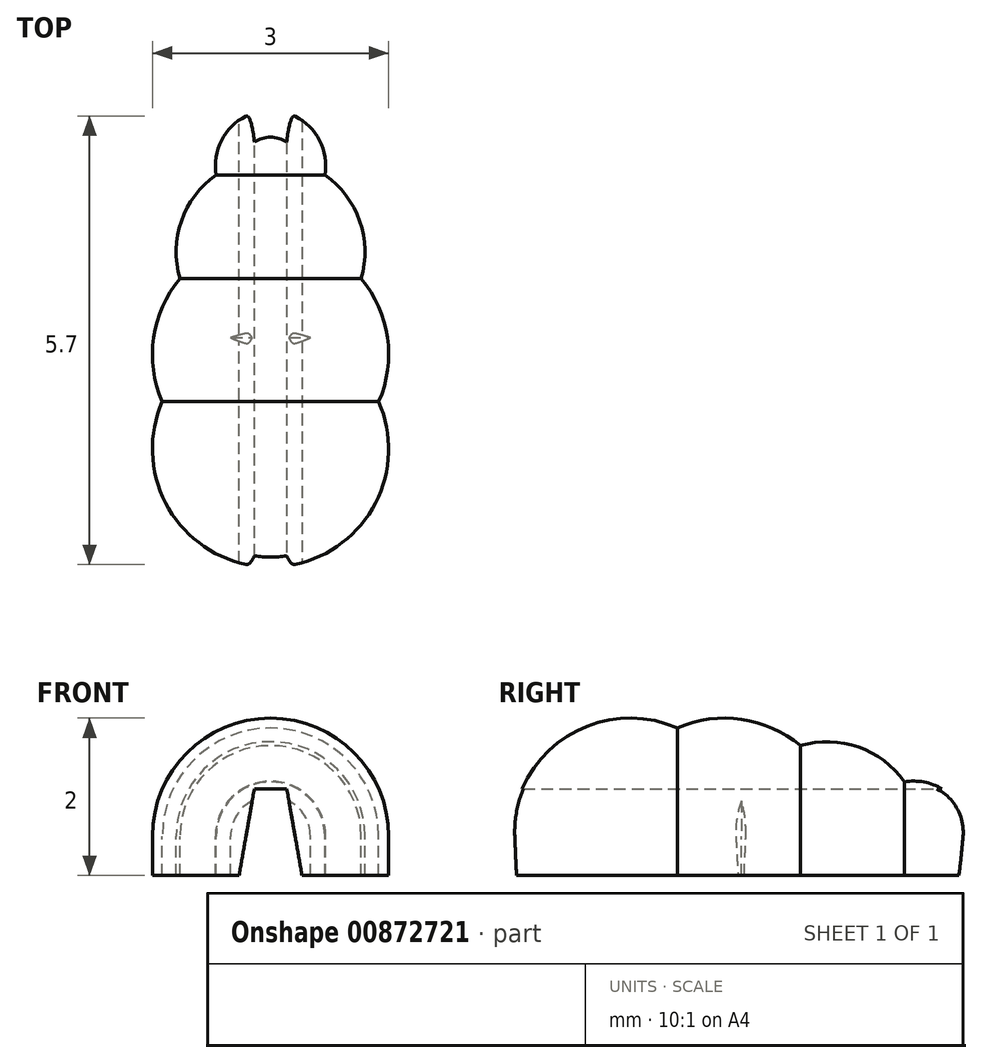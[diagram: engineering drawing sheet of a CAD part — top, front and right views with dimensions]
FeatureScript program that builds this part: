
annotation { "Feature Type Name" : "Feature", "Feature Type Description" : "" }
export const myFeature = defineFeature(function(context is Context, id is Id, definition is map)
    precondition{}
    {
        {
            var Q0;
            Q0=qCreatedBy(makeId("Top.planeOp"),FACE);
            var sketch = newSketch(context, id + "F0", { "sketchPlane" : qUnion([Q0])});
            skArc(sketch, "E0", {"start": v(0, -1.5) * mm, "mid": v(1.5, 0) * mm, "end": v(0, 1.5) * mm});
            skArc(sketch, "E1", {"start": v(0, -2.7) * mm, "mid": v(1.5, -1.2) * mm, "end": v(0, 0.3) * mm});
            skLineSegment(sketch, "E2", {"start": v(0, 3.1) * mm, "end": v(0, -4.3) * mm});
            skArc(sketch, "E3", {"start": v(0, 0.1) * mm, "mid": v(1.2, 1.3) * mm, "end": v(0, 2.5) * mm});
            skArc(sketch, "E4", {"start": v(0, -3.7) * mm, "mid": v(1.2, -2.5) * mm, "end": v(0, -1.3) * mm});
            skArc(sketch, "E5", {"start": v(0, 1.7) * mm, "mid": v(0.7, 2.4) * mm, "end": v(0, 3.1) * mm});
            skArc(sketch, "E6", {"start": v(0, -4.3) * mm, "mid": v(0.7, -3.6) * mm, "end": v(0, -2.9) * mm});
            skSolve(sketch);
        }
        {
            var Q0;
            {var subQ0=sQuery(id+"F0.wireOp",EDGE,"E2");var subQ1=sQuery(id+"F0.wireOp",EDGE,"E0");var subQ2=makeQuery(id+"F0.imprint","INTERSECT",VERTEX,{"disambiguationData":[OD(1.0)],"derivedFrom":[subQ1,subQ0]});Q0=makeQuery(id+"F0.imprint","IMPRINT",FACE,{"disambiguationData":[TD([[makeQuery(id+"F0.imprint","IMPRINT",EDGE,{"disambiguationData":[TD([[subQ2,1.0]])],"derivedFrom":subQ1}),1.0]])]});}
            var Q1;
            {var subQ0=sQuery(id+"F0.wireOp",EDGE,"E2");var subQ1=sQuery(id+"F0.wireOp",EDGE,"E0");var subQ2=makeQuery(id+"F0.imprint","INTERSECT",VERTEX,{"disambiguationData":[OD(0.0)],"derivedFrom":[subQ1,subQ0]});Q1=makeQuery(id+"F0.imprint","IMPRINT",FACE,{"disambiguationData":[TD([[makeQuery(id+"F0.imprint","IMPRINT",EDGE,{"disambiguationData":[TD([[subQ2,-1.0]])],"derivedFrom":subQ1}),1.0]])]});}
            var Q2;
            {var subQ0=sQuery(id+"F0.wireOp",EDGE,"E2");var subQ1=sQuery(id+"F0.wireOp",EDGE,"E0");var subQ2=makeQuery(id+"F0.imprint","INTERSECT",VERTEX,{"disambiguationData":[OD(0.0)],"derivedFrom":[subQ1,subQ0]});Q2=makeQuery(id+"F0.imprint","IMPRINT",FACE,{"disambiguationData":[TD([[makeQuery(id+"F0.imprint","IMPRINT",EDGE,{"disambiguationData":[TD([[subQ2,-1.0]])],"derivedFrom":subQ1}),-1.0]])]});}
            var Q3;
            {var subQ0=sQuery(id+"F0.wireOp",EDGE,"E2");var subQ1=sQuery(id+"F0.wireOp",EDGE,"E0");var subQ2=makeQuery(id+"F0.imprint","INTERSECT",VERTEX,{"disambiguationData":[OD(1.0)],"derivedFrom":[subQ1,subQ0]});Q3=makeQuery(id+"F0.imprint","IMPRINT",FACE,{"disambiguationData":[TD([[makeQuery(id+"F0.imprint","IMPRINT",EDGE,{"disambiguationData":[TD([[subQ2,1.0]])],"derivedFrom":subQ1}),-1.0]])]});}
            var Q4;
            {var subQ0=sQuery(id+"F0.wireOp",EDGE,"E1");var subQ1=sQuery(id+"F0.wireOp",EDGE,"E0");var subQ2=makeQuery(id+"F0.imprint","INTERSECT",VERTEX,{"derivedFrom":[subQ1,subQ0]});Q4=makeQuery(id+"F0.imprint","IMPRINT",FACE,{"disambiguationData":[TD([[makeQuery(id+"F0.imprint","IMPRINT",EDGE,{"disambiguationData":[TD([[subQ2,-1.0]])],"derivedFrom":subQ1}),1.0]])]});}
            var Q5;
            {var subQ3=sQuery(id+"F0.wireOp",EDGE,"E1");var subQ7=sQuery(id+"F0.wireOp",EDGE,"E0");var subQ8=makeQuery(id+"F0.imprint","INTERSECT",VERTEX,{"derivedFrom":[subQ7,subQ3]});Q5=makeQuery(id+"F0.imprint","IMPRINT",FACE,{"disambiguationData":[TD([[makeQuery(id+"F0.imprint","IMPRINT",EDGE,{"disambiguationData":[TD([[subQ8,1.0]])],"derivedFrom":subQ7}),1.0]])]});}
            var Q6;
            {var subQ0=sQuery(id+"F0.wireOp",EDGE,"E1");var subQ1=sQuery(id+"F0.wireOp",EDGE,"E0");var subQ2=makeQuery(id+"F0.imprint","INTERSECT",VERTEX,{"derivedFrom":[subQ1,subQ0]});Q6=makeQuery(id+"F0.imprint","IMPRINT",FACE,{"disambiguationData":[TD([[makeQuery(id+"F0.imprint","IMPRINT",EDGE,{"disambiguationData":[TD([[subQ2,1.0]])],"derivedFrom":subQ1}),-1.0]])]});}
            var Q7;
            {var subQ0=sQuery(id+"F0.wireOp",EDGE,"E2");var subQ1=sQuery(id+"F0.wireOp",EDGE,"E1");var subQ2=makeQuery(id+"F0.imprint","INTERSECT",VERTEX,{"disambiguationData":[OD(0.0)],"derivedFrom":[subQ1,subQ0]});Q7=makeQuery(id+"F0.imprint","IMPRINT",FACE,{"disambiguationData":[TD([[makeQuery(id+"F0.imprint","IMPRINT",EDGE,{"disambiguationData":[TD([[subQ2,-1.0]])],"derivedFrom":subQ1}),-1.0]])]});}
            var Q8;
            {var subQ0=sQuery(id+"F0.wireOp",EDGE,"E2");var subQ1=sQuery(id+"F0.wireOp",EDGE,"E1");var subQ2=makeQuery(id+"F0.imprint","INTERSECT",VERTEX,{"disambiguationData":[OD(1.0)],"derivedFrom":[subQ1,subQ0]});Q8=makeQuery(id+"F0.imprint","IMPRINT",FACE,{"disambiguationData":[TD([[makeQuery(id+"F0.imprint","IMPRINT",EDGE,{"disambiguationData":[TD([[subQ2,1.0]])],"derivedFrom":subQ1}),1.0]])]});}
            var Q9;
            {var subQ0=sQuery(id+"F0.wireOp",EDGE,"E3");var subQ1=sQuery(id+"F0.wireOp",EDGE,"E2");var subQ2=makeQuery(id+"F0.imprint","INTERSECT",VERTEX,{"disambiguationData":[OD(1.0)],"derivedFrom":[subQ1,subQ0]});Q9=makeQuery(id+"F0.imprint","IMPRINT",FACE,{"disambiguationData":[TD([[makeQuery(id+"F0.imprint","IMPRINT",EDGE,{"disambiguationData":[TD([[subQ2,1.0]])],"derivedFrom":subQ1}),1.0]])]});}
            var Q10;
            {var subQ0=sQuery(id+"F0.wireOp",EDGE,"E3");var subQ1=sQuery(id+"F0.wireOp",EDGE,"E2");var subQ2=makeQuery(id+"F0.imprint","INTERSECT",VERTEX,{"disambiguationData":[OD(1.0)],"derivedFrom":[subQ1,subQ0]});Q10=makeQuery(id+"F0.imprint","IMPRINT",FACE,{"disambiguationData":[TD([[makeQuery(id+"F0.imprint","IMPRINT",EDGE,{"disambiguationData":[TD([[subQ2,-1.0]])],"derivedFrom":subQ1}),1.0]])]});}
            var Q11;
            {var subQ0=sQuery(id+"F0.wireOp",EDGE,"E4");var subQ1=sQuery(id+"F0.wireOp",EDGE,"E2");var subQ2=makeQuery(id+"F0.imprint","INTERSECT",VERTEX,{"disambiguationData":[OD(0.0)],"derivedFrom":[subQ1,subQ0]});Q11=makeQuery(id+"F0.imprint","IMPRINT",FACE,{"disambiguationData":[TD([[makeQuery(id+"F0.imprint","IMPRINT",EDGE,{"disambiguationData":[TD([[subQ2,-1.0]])],"derivedFrom":subQ1}),1.0]])]});}
            var Q12;
            {var subQ0=sQuery(id+"F0.wireOp",EDGE,"E4");var subQ1=sQuery(id+"F0.wireOp",EDGE,"E2");var subQ2=makeQuery(id+"F0.imprint","INTERSECT",VERTEX,{"disambiguationData":[OD(0.0)],"derivedFrom":[subQ1,subQ0]});Q12=makeQuery(id+"F0.imprint","IMPRINT",FACE,{"disambiguationData":[TD([[makeQuery(id+"F0.imprint","IMPRINT",EDGE,{"disambiguationData":[TD([[subQ2,1.0]])],"derivedFrom":subQ1}),1.0]])]});}
            var Q13;
            Q13=sQuery(id+"F0.wireOp",EDGE,"E2");
            revolve(context, id + "F1", {"surfaceOperationType" : NewSurfaceOperationType.NEW, "entities" : qUnion([Q0, Q1, Q2, Q3, Q4, Q5, Q6, Q7, Q8, Q9, Q10, Q11, Q12]), "axis" : qUnion([Q13]), "revolveType" : RevolveType.ONE_DIRECTION, "angle" : 180 * degree});
        }
        {
            var Q0;
            Q0=makeQuery(id+"F1.opRevolve","CAP_FACE",FACE,{"disambiguationData":[OSD([sQuery(id+"F0.wireOp",EDGE,"E0"),sQuery(id+"F0.wireOp",EDGE,"E1"),sQuery(id+"F0.wireOp",EDGE,"E2"),sQuery(id+"F0.wireOp",EDGE,"E3"),sQuery(id+"F0.wireOp",EDGE,"E4"),sQuery(id+"F0.wireOp",EDGE,"E5"),sQuery(id+"F0.wireOp",EDGE,"E6")])],"isStart":false});
            var sketch = newSketch(context, id + "F2", { "sketchPlane" : qUnion([Q0])});
            skArc(sketch, "E7.0", {"start": v(-1.15, -0.96) * mm, "mid": v(-1.13, -1.7) * mm, "end": v(-0.69, -2.28) * mm});
            skArc(sketch, "E8.0.0", {"start": v(-0.69, -2.28) * mm, "mid": v(0, -3.1) * mm, "end": v(0.69, -2.28) * mm});
            skArc(sketch, "E8.0.1", {"start": v(0.69, -2.28) * mm, "mid": v(1.13, -1.7) * mm, "end": v(1.15, -0.96) * mm});
            skArc(sketch, "E8.0.2", {"start": v(1.15, -0.96) * mm, "mid": v(1.48, -0.21) * mm, "end": v(1.37, 0.6) * mm});
            skArc(sketch, "E8.0.3", {"start": v(1.37, 0.6) * mm, "mid": v(1.48, 1.41) * mm, "end": v(1.15, 2.16) * mm});
            skArc(sketch, "E8.0.4", {"start": v(1.15, 2.16) * mm, "mid": v(1.13, 2.9) * mm, "end": v(0.69, 3.48) * mm});
            skArc(sketch, "E8.0.5", {"start": v(0.69, 3.48) * mm, "mid": v(0, 4.3) * mm, "end": v(-0.69, 3.48) * mm});
            skArc(sketch, "E8.0.6", {"start": v(-0.69, 3.48) * mm, "mid": v(-1.13, 2.9) * mm, "end": v(-1.15, 2.16) * mm});
            skArc(sketch, "E8.0.7", {"start": v(-1.15, 2.16) * mm, "mid": v(-1.48, 1.41) * mm, "end": v(-1.37, 0.6) * mm});
            skArc(sketch, "E8.0.8", {"start": v(-1.37, 0.6) * mm, "mid": v(-1.48, -0.21) * mm, "end": v(-1.15, -0.96) * mm});
            skSolve(sketch);
        }
        {
            var Q0;
            Q0=makeQuery(id+"F2.imprint","IMPRINT",FACE,{"disambiguationData":[TD([[makeQuery(id+"F2.imprint","IMPRINT",EDGE,{"derivedFrom":sQuery(id+"F2.wireOp",EDGE,"E8.0.0")}),1.0]])]});
            extrude(context, id + "F3", {"entities" : qUnion([Q0]), "operationType" : NewBodyOperationType.ADD, "depth" : .5 * mm, "offsetDistance" : 25 * mm});
        }
        {
            var Q0;
            Q0=makeQuery(id+"F3.opExtrude","CAP_FACE",FACE,{"disambiguationData":[OSD([sQuery(id+"F2.wireOp",EDGE,"E8.0.0"),sQuery(id+"F2.wireOp",EDGE,"E8.0.1"),sQuery(id+"F2.wireOp",EDGE,"E8.0.2"),sQuery(id+"F2.wireOp",EDGE,"E8.0.3"),sQuery(id+"F2.wireOp",EDGE,"E8.0.4"),sQuery(id+"F2.wireOp",EDGE,"E8.0.5"),sQuery(id+"F2.wireOp",EDGE,"E8.0.6"),sQuery(id+"F2.wireOp",EDGE,"E8.0.7"),sQuery(id+"F2.wireOp",EDGE,"E8.0.8"),sQuery(id+"F2.wireOp",EDGE,"E7.0")])],"isStart":false});
            var sketch = newSketch(context, id + "F4", { "sketchPlane" : qUnion([Q0])});
            skLineSegment(sketch, "E9.bottom", {"start": v(-0.4, 6.07) * mm, "end": v(0.4, 6.07) * mm});
            skLineSegment(sketch, "E9.top", {"start": v(-0.4, -6.07) * mm, "end": v(0.4, -6.07) * mm});
            skLineSegment(sketch, "E9.left", {"start": v(-0.4, 6.07) * mm, "end": v(-0.4, -6.07) * mm});
            skLineSegment(sketch, "E9.right", {"start": v(0.4, 6.07) * mm, "end": v(0.4, -6.07) * mm});
            skPoint(sketch, "E9.middle", {"position": v(0, 0) * mm});
            skSolve(sketch);
        }
        {
            var Q0;
            {var subQ0=sQuery(id+"F4.wireOp",EDGE,"E9.left");var subQ1=makeQuery(id+"F3.opExtrude","CAP_EDGE",EDGE,{"disambiguationData":[OSD([sQuery(id+"F2.wireOp",EDGE,"E8.0.5")])],"isStart":false});var subQ2=makeQuery(id+"F4.imprint","INTERSECT",VERTEX,{"derivedFrom":[subQ1,subQ0]});Q0=makeQuery(id+"F4.imprint","IMPRINT",FACE,{"disambiguationData":[TD([[makeQuery(id+"F4.imprint","IMPRINT",EDGE,{"disambiguationData":[TD([[subQ2,-1.0]])],"derivedFrom":subQ0}),1.0]])]});}
            var Q1;
            {var subQ0=sQuery(id+"F4.wireOp",EDGE,"E9.top");Q1=makeQuery(id+"F4.imprint","IMPRINT",FACE,{"disambiguationData":[TD([[makeQuery(id+"F4.imprint","IMPRINT",EDGE,{"derivedFrom":subQ0}),1.0]])]});}
            var Q2;
            {var subQ0=sQuery(id+"F4.wireOp",EDGE,"E9.bottom");Q2=makeQuery(id+"F4.imprint","IMPRINT",FACE,{"disambiguationData":[TD([[makeQuery(id+"F4.imprint","IMPRINT",EDGE,{"derivedFrom":subQ0}),-1.0]])]});}
            extrude(context, id + "F5", {"entities" : qUnion([Q0, Q1, Q2]), "operationType" : NewBodyOperationType.REMOVE, "oppositeDirection" : true, "depth" : 1.1 * mm, "offsetDistance" : 25 * mm, "hasDraft" : true, "draftAngle" : 10 * degree, "draftPullDirection" : true});
        }
    });
